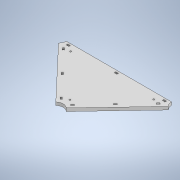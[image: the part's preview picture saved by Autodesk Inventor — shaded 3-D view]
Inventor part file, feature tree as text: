
AUTODESK INVENTOR PART (.ipt)
format: ipt  version: 2020 (Build 240168000, 168)  size: 156,160 bytes
history: native  units: in
note: dims shown in document units (in); Inventor stores cm internally (conversion verified against a paired STEP export)
features: extrude x1, sketch x1
ambient origin geometry x8: Origin, YZ Plane, XZ Plane, XY Plane, X Axis, Y Axis, Z Axis, Center Point
bodies: Solid1 (feature_tree)
feature tree (2):
  extrude  "Extrusion1"  [1 undecoded]
  sketch  "Sketch1"  dims[d0=0.1575in d1=0.0in]
note: 1 required parameter value undecoded (feature->parameter linkage not recoverable at this tier; creation-order binding heuristic only, values carry confidence <= 0.55)
